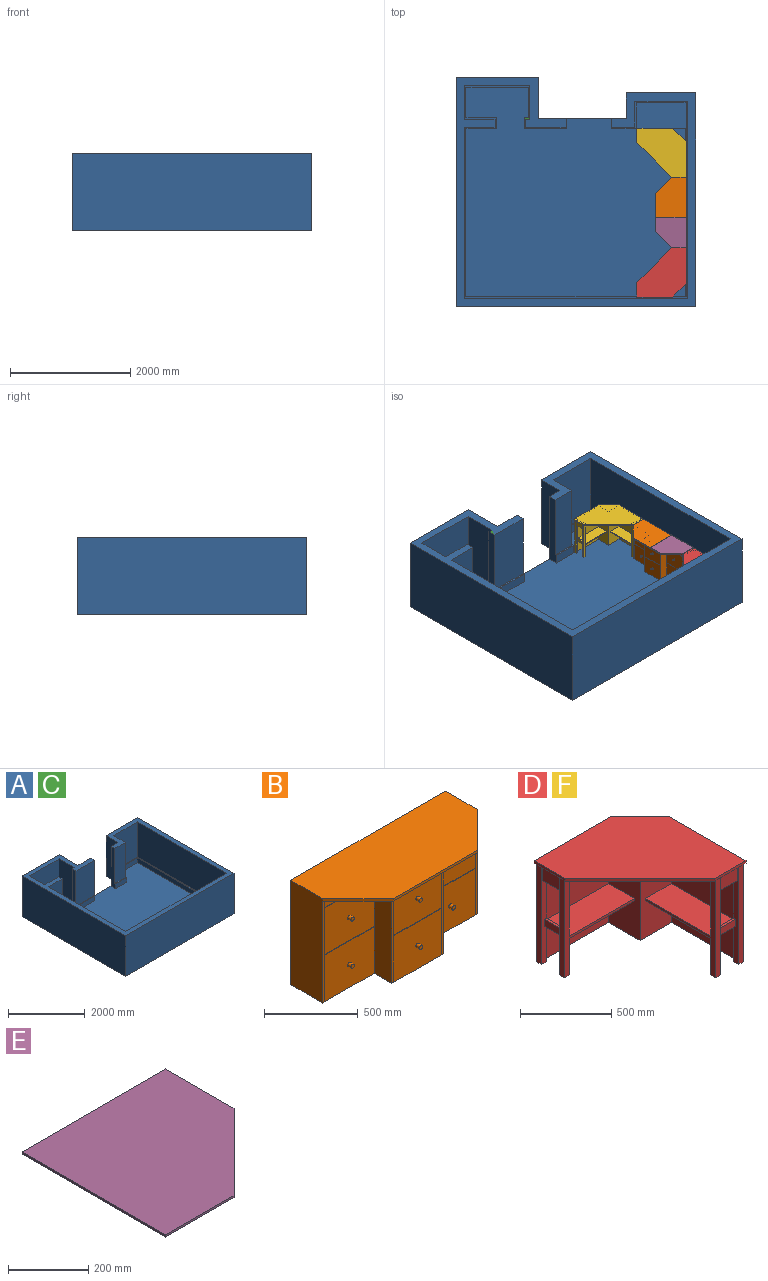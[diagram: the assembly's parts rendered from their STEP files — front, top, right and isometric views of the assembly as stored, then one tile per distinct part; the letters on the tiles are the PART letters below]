
ASSEMBLY  parts=6 mates=4
PART A: 44 faces, bbox 3987.8x3816.4x1295.4 mm
  f0: plane 1117.6x431.8mm, normal (1,0,0), area 482579.7mm2, adj f1,f24,f25,f43
  f1: plane 1117.6x876.3mm, normal (0,-1,0), area 979352.9mm2, adj f0,f2,f25,f43
  f2: plane 3276.6x1117.6mm, normal (-1,0,0), area 3661928.2mm2, adj f1,f3,f25,f43
  f3: plane 3708.4x1117.6mm, normal (0,1,0), area 4144507.8mm2, adj f2,f4,f25,f43
  f4: plane 2844.8x1117.6mm, normal (1,0,0), area 3179348.5mm2, adj f3,f5,f25,f43
  f5: plane 1117.6x508mm, normal (0,-1,0), area 567740.8mm2, adj f4,f6,f25,f43
  f6: plane 1117.6x133.35mm, normal (1,0,0), area 149032mm2, adj f5,f7,f25,f43
  f7: plane 1117.6x508mm, normal (0,1,0), area 567740.8mm2, adj f6,f8,f25,f43
  f8: plane 1117.6x558.8mm, normal (1,0,0), area 624514.9mm2, adj f7,f9,f25,f43
  f9: plane 1117.6x1085.85mm, normal (0,-1,0), area 1213546mm2, adj f8,f10,f25,f43
  f10: plane 1117.6x558.8mm, normal (-1,0,0), area 624514.9mm2, adj f9,f11,f25,f43
  f11: plane 1117.6x69.85mm, normal (0,1,0), area 78064.4mm2, adj f10,f12,f25,f43
  f12: plane 1117.6x133.35mm, normal (-1,0,0), area 149032mm2, adj f11,f13,f25,f43
  f13: plane 1117.6x673.1mm, normal (0,-1,0), area 752256.6mm2, adj f12,f14,f25,f43
  f14: plane 1270x165.1mm, normal (1,0,0), area 181290mm2, adj f13,f22,f25,f26,f42,f43
  f15: plane 1295.4x692.15mm, normal (1,0,0), area 896611.1mm2, adj f16,f22,f25,f27
  f16: plane 1365.25x1295.4mm, normal (0,1,0), area 1768544.9mm2, adj f15,f17,f25,f27
  f17: plane 3816.35x1295.4mm, normal (-1,0,0), area 4943699.8mm2, adj f16,f18,f25,f27
  f18: plane 3987.8x1295.4mm, normal (0,-1,0), area 5165796.1mm2, adj f17,f19,f25,f27
  f19: plane 3556x1295.4mm, normal (1,0,0), area 4606442.4mm2, adj f18,f20,f25,f27
  f20: plane 1295.4x1155.7mm, normal (0,1,0), area 1497093.8mm2, adj f19,f21,f25,f27
  f21: plane 1295.4x431.8mm, normal (-1,0,0), area 559353.7mm2, adj f20,f22,f25,f27
  f22: plane 1466.85x1295.4mm, normal (0,1,0), area 940482mm2, adj f14,f15,f21,f23,f25,f26,f27
  f23: plane 1270x165.1mm, normal (-1,0,0), area 181290mm2, adj f22,f24,f25,f26,f28,f43
  f24: plane 1117.6x387.35mm, normal (0,-1,0), area 432902.4mm2, adj f0,f23,f25,f43
  f25: plane 3987.8x3816.35mm, normal (0,0,1), area 2194552.1mm2, adj f0,f1,f2,f3,f4,f5,f6,f7
  f26: plane 3657.6x3486.15mm, normal (0,0,1), area 11310541.9mm2, adj f14,f22,f23,f28,f29,f30,f31,f32
  f27: plane 3987.8x3816.35mm, normal (0,0,-1), area 13902673.8mm2, adj f15,f16,f17,f18,f19,f20,f21,f22
  f28: plane 412.75x152.4mm, normal (0,-1,0), area 62903.1mm2, adj f23,f26,f29,f43
  f29: plane 431.8x152.4mm, normal (1,0,0), area 65806.3mm2, adj f26,f28,f30,f43
  f30: plane 825.5x152.4mm, normal (0,-1,0), area 125806.2mm2, adj f26,f29,f31,f43
  f31: plane 3225.8x152.4mm, normal (-1,0,0), area 491611.9mm2, adj f26,f30,f32,f43
  f32: plane 3657.6x152.4mm, normal (0,1,0), area 557418.2mm2, adj f26,f31,f33,f43
  f33: plane 2794x152.4mm, normal (1,0,0), area 425805.6mm2, adj f26,f32,f34,f43
  f34: plane 508x152.4mm, normal (0,-1,0), area 77419.2mm2, adj f26,f33,f35,f43
  f35: plane 184.15x152.4mm, normal (1,0,0), area 28064.5mm2, adj f26,f34,f36,f43
  f36: plane 508x152.4mm, normal (0,1,0), area 77419.2mm2, adj f26,f35,f37,f43
  f37: plane 508x152.4mm, normal (1,0,0), area 77419.2mm2, adj f26,f36,f38,f43
  f38: plane 1035.05x152.4mm, normal (0,-1,0), area 157741.6mm2, adj f26,f37,f39,f43
  f39: plane 508x152.4mm, normal (-1,0,0), area 77419.2mm2, adj f26,f38,f40,f43
  f40: plane 152.4x69.85mm, normal (0,1,0), area 10645.1mm2, adj f26,f39,f41,f43
  f41: plane 184.15x152.4mm, normal (-1,0,0), area 28064.5mm2, adj f26,f40,f42,f43
  f42: plane 698.5x152.4mm, normal (0,-1,0), area 106451.4mm2, adj f14,f26,f41,f43
  f43: plane 3708.4x3536.95mm, normal (0,0,1), area 397579.8mm2, adj f0,f1,f2,f3,f4,f5,f6,f7
PART B: 65 faces, bbox 1168.4x508x682.6 mm
  f0: plane 304.8x0.13mm, normal (-1,0,0), area 38.7mm2, adj f24,f30,f62,f63
  f1: plane 50.8x0.13mm, normal (-1,0,0), area 6.5mm2, adj f10,f24,f31,f61
  f2: plane 50.8x0.13mm, normal (1,0,0), area 6.5mm2, adj f10,f23,f28,f59
  f3: plane 666.75x133.48mm, normal (-1,0,0), area 88995mm2, adj f10,f22,f23,f25,f26,f27,f28,f57
  f4: plane 304.8x0.13mm, normal (1,0,0), area 38.7mm2, adj f23,f27,f58,f60
  f5: plane 50.8x0.13mm, normal (-1,0,0), area 6.5mm2, adj f10,f22,f34,f55
  f6: plane 50.8x0.13mm, normal (1,0,0), area 6.5mm2, adj f10,f22,f34,f55
  f7: plane 304.8x0.13mm, normal (-1,0,0), area 38.7mm2, adj f22,f33,f54,f56
  f8: plane 304.8x0.13mm, normal (1,0,0), area 38.7mm2, adj f22,f33,f54,f56
  f9: plane 304.8x0.13mm, normal (-1,0,0), area 38.7mm2, adj f22,f25,f32,f53
  f10: plane 1168.4x266.83mm, normal (0,0,-1), area 188547.2mm2, adj f1,f2,f3,f5,f6,f13,f18,f19
  f11: plane 304.8x0.13mm, normal (1,0,0), area 38.7mm2, adj f22,f25,f32,f53
  f12: plane 304.8x0.13mm, normal (-1,0,0), area 38.7mm2, adj f24,f25,f29,f64
  f13: plane 666.75x133.48mm, normal (1,0,0), area 88995mm2, adj f10,f22,f24,f25,f29,f30,f31,f61
  f14: plane 304.8x0.13mm, normal (1,0,0), area 38.7mm2, adj f23,f25,f26,f57
  f15: plane 682.63x241.3mm, normal (1,0,0), area 164717.4mm2, adj f16,f20,f21,f24,f25
  f16: plane 1168.4x682.63mm, normal (0,1,0), area 797579mm2, adj f15,f17,f21,f25
  f17: plane 682.63x241.3mm, normal (-1,0,0), area 164717.4mm2, adj f16,f18,f21,f23,f25
  f18: plane 266.7x266.7mm, normal (-0.71,-0.71,0), area 5987.6mm2, adj f10,f17,f19,f21
  f19: plane 635x15.88mm, normal (0,-1,0), area 10080.6mm2, adj f10,f18,f20,f21
  f20: plane 266.7x266.7mm, normal (0.71,-0.71,0), area 5987.6mm2, adj f10,f15,f19,f21
  f21: plane 1168.4x508mm, normal (0,0,1), area 522418.3mm2, adj f15,f16,f17,f18,f19,f20
  f22: plane 666.75x390.53mm, normal (0,-1,0), area 23447.5mm2, adj f3,f5,f6,f7,f8,f9,f10,f11
  f23: plane 666.75x388.94mm, normal (0,-1,0), area 12953.6mm2, adj f2,f3,f4,f10,f14,f17,f25,f57
  f24: plane 666.75x388.94mm, normal (0,-1,0), area 12953.6mm2, adj f0,f1,f10,f12,f13,f15,f25,f61
  f25: plane 1168.4x374.65mm, normal (0,0,-1), area 333871.1mm2, adj f3,f9,f11,f12,f13,f14,f15,f16
  f26: plane 373.06x304.8mm, normal (0,-1,0), area 113202.7mm2, adj f3,f14,f25,f35,f57
  f27: plane 373.06x304.8mm, normal (0,-1,0), area 113202.7mm2, adj f3,f4,f37,f58,f60
  f28: plane 373.06x50.8mm, normal (0,-1,0), area 18444.9mm2, adj f2,f3,f10,f39,f59
  f29: plane 373.06x304.8mm, normal (0,-1,0), area 113202.7mm2, adj f12,f13,f25,f47,f64
  f30: plane 373.06x304.8mm, normal (0,-1,0), area 113202.7mm2, adj f0,f13,f49,f62,f63
  f31: plane 373.06x50.8mm, normal (0,-1,0), area 18444.9mm2, adj f1,f10,f13,f51,f61
  f32: plane 358.78x304.8mm, normal (0,-1,0), area 108847.9mm2, adj f9,f11,f25,f41,f53
  f33: plane 358.78x304.8mm, normal (0,-1,0), area 108847.9mm2, adj f7,f8,f43,f54,f56
  f34: plane 358.78x50.8mm, normal (0,-1,0), area 17719.1mm2, adj f5,f6,f10,f45,f55
  f35: cylinder r=12.7mm len=25.4mm, axis (0,1,0), area 2026.8mm2, adj f26,f36
  f36: plane 25.4x25.4mm, normal (0,-1,0), area 506.7mm2, adj f35
  f37: cylinder r=12.7mm len=25.4mm, axis (0,1,0), area 2026.8mm2, adj f27,f38
  f38: plane 25.4x25.4mm, normal (0,-1,0), area 506.7mm2, adj f37
  f39: cylinder r=12.7mm len=25.4mm, axis (0,1,0), area 2026.8mm2, adj f28,f40
  f40: plane 25.4x25.4mm, normal (0,-1,0), area 506.7mm2, adj f39
  f41: cylinder r=12.7mm len=25.4mm, axis (0,1,0), area 2026.8mm2, adj f32,f42
  f42: plane 25.4x25.4mm, normal (0,-1,0), area 506.7mm2, adj f41
  f43: cylinder r=12.7mm len=25.4mm, axis (0,1,0), area 2026.8mm2, adj f33,f44
  f44: plane 25.4x25.4mm, normal (0,-1,0), area 506.7mm2, adj f43
  f45: cylinder r=12.7mm len=25.4mm, axis (0,1,0), area 2026.8mm2, adj f34,f46
  f46: plane 25.4x25.4mm, normal (0,-1,0), area 506.7mm2, adj f45
  f47: cylinder r=12.7mm len=25.4mm, axis (0,1,0), area 2026.8mm2, adj f29,f48
  f48: plane 25.4x25.4mm, normal (0,-1,0), area 506.7mm2, adj f47
  f49: cylinder r=12.7mm len=25.4mm, axis (0,1,0), area 2026.8mm2, adj f30,f50
  f50: plane 25.4x25.4mm, normal (0,-1,0), area 506.7mm2, adj f49
  f51: cylinder r=12.7mm len=25.4mm, axis (0,1,0), area 2026.8mm2, adj f31,f52
  f52: plane 25.4x25.4mm, normal (0,-1,0), area 506.7mm2, adj f51
  f53: plane 358.78x0.13mm, normal (0,0,-1), area 45.6mm2, adj f9,f11,f22,f32
  f54: plane 358.78x0.13mm, normal (0,0,1), area 45.6mm2, adj f7,f8,f22,f33
  f55: plane 358.78x0.13mm, normal (0,0,1), area 45.6mm2, adj f5,f6,f22,f34
  f56: plane 358.78x0.13mm, normal (0,0,-1), area 45.6mm2, adj f7,f8,f22,f33
  f57: plane 373.06x0.13mm, normal (0,0,-1), area 47.4mm2, adj f3,f14,f23,f26
  f58: plane 373.06x0.13mm, normal (0,0,1), area 47.4mm2, adj f3,f4,f23,f27
  f59: plane 373.06x0.13mm, normal (0,0,1), area 47.4mm2, adj f2,f3,f23,f28
  f60: plane 373.06x0.13mm, normal (0,0,-1), area 47.4mm2, adj f3,f4,f23,f27
  f61: plane 373.06x0.13mm, normal (0,0,1), area 47.4mm2, adj f1,f13,f24,f31
  f62: plane 373.06x0.13mm, normal (0,0,-1), area 47.4mm2, adj f0,f13,f24,f30
  f63: plane 373.06x0.13mm, normal (0,0,1), area 47.4mm2, adj f0,f13,f24,f30
  f64: plane 373.06x0.13mm, normal (0,0,-1), area 47.4mm2, adj f12,f13,f24,f29
PART C: same geometry as A
PART D: 54 faces, bbox 820.5x820.5x682.6 mm
  f0: plane 666.75x242.68mm, normal (1,0,0), area 161794.5mm2, adj f1,f12,f20,f34,f52,f53
  f1: plane 666.75x242.68mm, normal (0,1,0), area 161794.5mm2, adj f0,f12,f20,f35,f51,f53
  f2: plane 244.48x38.1mm, normal (0,1,0), area 9314.5mm2, adj f9,f10,f39,f47
  f3: plane 244.48x22.23mm, normal (0,1,0), area 5433.5mm2, adj f4,f8,f12,f47
  f4: plane 504.83x244.48mm, normal (-1,0,0), area 123417.1mm2, adj f3,f12,f23,f47
  f5: plane 504.83x244.48mm, normal (0,-1,0), area 123417.1mm2, adj f6,f12,f24,f43
  f6: plane 244.48x22.23mm, normal (1,0,0), area 5433.5mm2, adj f5,f12,f27,f43
  f7: plane 406.4x200.03mm, normal (1,0,0), area 28951.6mm2, adj f20,f25,f27,f29,f30,f41,f49
  f8: plane 666.75x38.1mm, normal (-1,0,0), area 22933.4mm2, adj f3,f11,f12,f20,f21,f36,f37,f45
  f9: plane 666.75x38.1mm, normal (1,0,0), area 22933.4mm2, adj f2,f10,f11,f20,f21,f37,f38,f45
  f10: plane 38.1x38.1mm, normal (0,0,-1), area 1451.6mm2, adj f2,f9,f38,f39
  f11: plane 139.7x107.95mm, normal (0,1,0), area 15080.6mm2, adj f8,f9,f20,f46
  f12: plane 801.48x801.48mm, normal (0,0,-1), area 28419.3mm2, adj f0,f1,f3,f4,f5,f6,f8,f23
  f13: plane 596.9x15.88mm, normal (0,1,0), area 9475.8mm2, adj f14,f18,f19,f20
  f14: plane 241.3x15.88mm, normal (-1,0,0), area 3830.6mm2, adj f13,f15,f19,f20
  f15: plane 579.23x579.23mm, normal (-0.71,-0.71,0), area 13004mm2, adj f14,f16,f19,f20
  f16: plane 241.3x15.88mm, normal (0,-1,0), area 3830.6mm2, adj f15,f17,f19,f20
  f17: plane 596.9x15.88mm, normal (1,0,0), area 9475.8mm2, adj f16,f18,f19,f20
  f18: plane 223.63x223.63mm, normal (0.71,0.71,0), area 5020.6mm2, adj f13,f17,f19,f20
  f19: plane 820.53x820.53mm, normal (0,0,1), area 480507.7mm2, adj f13,f14,f15,f16,f17,f18
  f20: plane 820.53x820.53mm, normal (0,0,-1), area 446280.6mm2, adj f0,f1,f7,f8,f9,f11,f13,f14
  f21: plane 406.4x200.03mm, normal (0,1,0), area 28951.6mm2, adj f8,f9,f20,f22,f39,f45,f50
  f22: plane 504.83x406.4mm, normal (-1,0,0), area 205160.9mm2, adj f20,f21,f23,f50
  f23: plane 666.75x242.68mm, normal (0,-1,0), area 158629.2mm2, adj f4,f12,f20,f22,f24,f39,f47,f50
  f24: plane 666.75x242.68mm, normal (-1,0,0), area 158629.2mm2, adj f5,f12,f20,f23,f25,f30,f43,f49
  f25: plane 504.83x406.4mm, normal (0,-1,0), area 205160.9mm2, adj f7,f20,f24,f49
  f26: plane 244.48x38.1mm, normal (1,0,0), area 9314.5mm2, adj f29,f30,f40,f43
  f27: plane 666.75x38.1mm, normal (0,-1,0), area 22933.4mm2, adj f6,f7,f12,f20,f28,f32,f33,f41
  f28: plane 139.7x107.95mm, normal (1,0,0), area 15080.6mm2, adj f20,f27,f29,f42
  f29: plane 666.75x38.1mm, normal (0,1,0), area 22933.4mm2, adj f7,f20,f26,f28,f31,f32,f40,f41
  f30: plane 666.75x542.93mm, normal (0,-1,0), area 33417.3mm2, adj f7,f20,f24,f26,f31,f40,f43,f49
  f31: plane 666.75x38.1mm, normal (-1,0,0), area 25403.2mm2, adj f20,f29,f30,f40
  f32: plane 139.7x107.95mm, normal (-1,0,0), area 15080.6mm2, adj f20,f27,f29,f42
  f33: plane 666.75x38.1mm, normal (-1,0,0), area 25403.2mm2, adj f12,f20,f27,f34
  f34: plane 801.48x666.75mm, normal (0,1,0), area 373350.4mm2, adj f0,f12,f20,f33,f35,f53
  f35: plane 801.48x666.75mm, normal (1,0,0), area 373350.4mm2, adj f1,f12,f20,f34,f36,f53
  f36: plane 666.75x38.1mm, normal (0,-1,0), area 25403.2mm2, adj f8,f12,f20,f35
  f37: plane 139.7x107.95mm, normal (0,-1,0), area 15080.6mm2, adj f8,f9,f20,f46
  f38: plane 666.75x38.1mm, normal (0,-1,0), area 25403.2mm2, adj f9,f10,f20,f39
  f39: plane 666.75x542.93mm, normal (-1,0,0), area 33417.3mm2, adj f2,f10,f20,f21,f23,f38,f47,f50
  f40: plane 38.1x38.1mm, normal (0,0,-1), area 1451.6mm2, adj f26,f29,f30,f31
  f41: plane 139.7x15.88mm, normal (0,0,1), area 2217.7mm2, adj f7,f27,f29,f44
  f42: plane 139.7x15.88mm, normal (0,0,-1), area 2217.7mm2, adj f27,f28,f29,f32
  f43: plane 520.7x200.03mm, normal (0,0,-1), area 103195.4mm2, adj f5,f6,f24,f26,f27,f29,f30,f44
  f44: plane 139.7x47.63mm, normal (-1,0,0), area 6653.2mm2, adj f27,f29,f41,f43
  f45: plane 139.7x15.88mm, normal (0,0,1), area 2217.7mm2, adj f8,f9,f21,f48
  f46: plane 139.7x15.88mm, normal (0,0,-1), area 2217.7mm2, adj f8,f9,f11,f37
  f47: plane 520.7x200.03mm, normal (0,0,-1), area 103195.4mm2, adj f2,f3,f4,f8,f9,f23,f39,f48
  f48: plane 139.7x47.63mm, normal (0,-1,0), area 6653.2mm2, adj f8,f9,f45,f47
  f49: plane 504.83x200.03mm, normal (0,0,1), area 100977.6mm2, adj f7,f24,f25,f30
  f50: plane 504.83x200.03mm, normal (0,0,1), area 100977.6mm2, adj f21,f22,f23,f39
  f51: plane 239.5x3.18mm, normal (-1,0,0), area 760.4mm2, adj f1,f12,f52,f53
  f52: plane 239.5x3.18mm, normal (0,-1,0), area 760.4mm2, adj f0,f12,f51,f53
  f53: plane 242.68x242.68mm, normal (0,0,1), area 1530.9mm2, adj f0,f1,f34,f35,f51,f52
PART E: 7 faces, bbox 508x508x6.4 mm
  f0: plane 508x6.35mm, normal (0,1,0), area 3225.8mm2, adj f1,f4,f5,f6
  f1: plane 508x6.35mm, normal (-1,0,0), area 3225.8mm2, adj f0,f2,f5,f6
  f2: plane 241.3x6.35mm, normal (0,-1,0), area 1532.3mm2, adj f1,f3,f5,f6
  f3: plane 266.7x266.7mm, normal (0.71,-0.71,0), area 2395mm2, adj f2,f4,f5,f6
  f4: plane 241.3x6.35mm, normal (1,0,0), area 1532.3mm2, adj f0,f3,f5,f6
  f5: plane 508x508mm, normal (0,0,1), area 222499.6mm2, adj f0,f1,f2,f3,f4
  f6: plane 508x508mm, normal (0,0,-1), area 222499.6mm2, adj f0,f1,f2,f3,f4
PART F: same geometry as D
PLACE A t=(-924.9,634.4,-591.85)mm
PLACE B rot(axis=(0,0,-1),90deg) t=(1561.79,-76.57,71.73)mm
PLACE C t=(-924.9,634.4,-591.85)mm
PLACE D rot(axis=(0,0,-1),90deg) t=(1486.04,-1080.6,71.73)mm
PLACE E rot(axis=(0,0,-1),90deg) t=(1561.79,-76.57,71.73)mm
PLACE F rot(axis=(0,0,-1),0deg) t=(1415.09,998.42,71.73)mm
MATE fastened E.f6 <-> B.f21  axis (0,0,-1) through (1815.79,-660.77,87.6)mm
MATE fastened B.f15 <-> D.f14  axis (0,-1,0) through (1815.79,-660.77,87.6)mm
MATE fastened F.f16 <-> B.f17  axis (0,-1,0) through (1815.79,507.63,87.6)mm
MATE fastened D.f53 <-> A.f26  axis (0,0,1) through (1812.61,-1478.12,-591.85)mm
